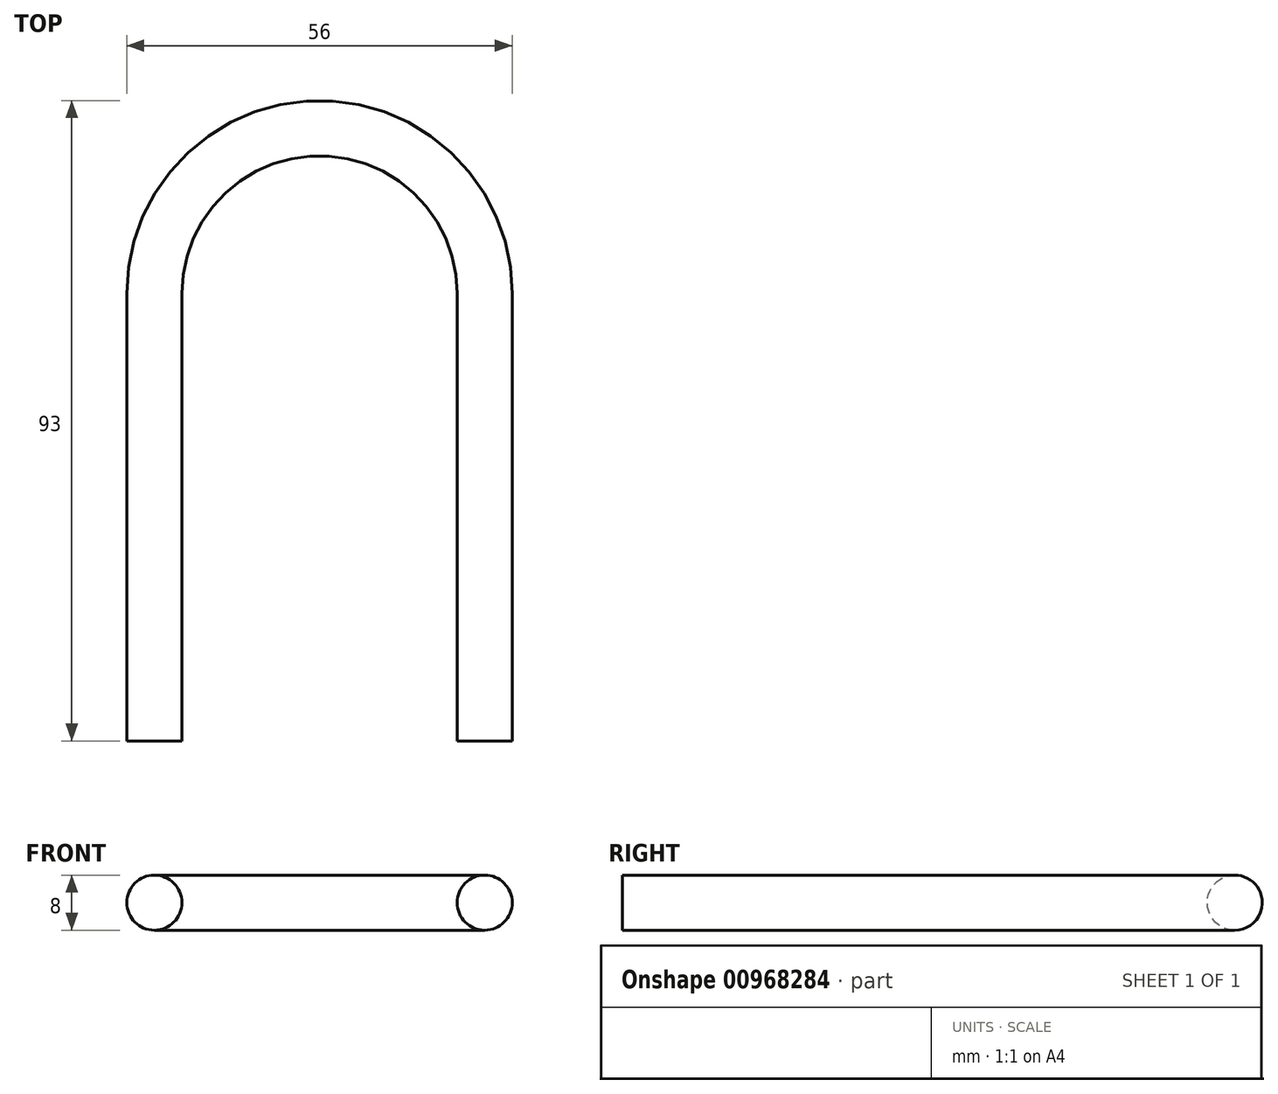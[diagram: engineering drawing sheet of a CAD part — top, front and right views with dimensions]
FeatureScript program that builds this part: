
annotation { "Feature Type Name" : "Feature", "Feature Type Description" : "" }
export const myFeature = defineFeature(function(context is Context, id is Id, definition is map)
    precondition{}
    {
        {
            var Q0;
            Q0=qCreatedBy(makeId("Front.planeOp"),FACE);
            var sketch = newSketch(context, id + "F0", { "sketchPlane" : qUnion([Q0])});
            skLineSegment(sketch, "E0", {"start": v(-20, 0) * mm, "end": v(20, 0) * mm, "construction": true});
            skCircle(sketch, "E1", {"center": v(24, 0) * mm, "radius": 4 * mm});
            skLineSegment(sketch, "E2", {"start": v(0, 33.76) * mm, "end": v(0, -41.5) * mm, "construction": true});
            skSolve(sketch);
        }
        {
            var Q0;
            Q0 = qSketchRegion(id + "F0", true);
            var Q1;
            Q1=sQuery(id+"F0.wireOp",EDGE,"E2");
            revolve(context, id + "F1", {"surfaceOperationType" : NewSurfaceOperationType.NEW, "entities" : qUnion([Q0]), "axis" : qUnion([Q1]), "revolveType" : RevolveType.ONE_DIRECTION, "oppositeDirection" : true, "angle" : 180 * degree});
        }
        {
            var Q0;
            Q0=makeQuery(id+"F1.opRevolve","CAP_FACE",FACE,{"disambiguationData":[OSD([sQuery(id+"F0.wireOp",EDGE,"E1")])],"isStart":false});
            var Q1;
            Q1=makeQuery(id+"F1.opRevolve","CAP_FACE",FACE,{"disambiguationData":[OSD([sQuery(id+"F0.wireOp",EDGE,"E1")])],"isStart":true});
            extrude(context, id + "F2", {"entities" : qUnion([Q0, Q1]), "operationType" : NewBodyOperationType.ADD, "depth" : 65 * mm, "offsetDistance" : 25 * mm});
        }
    });
